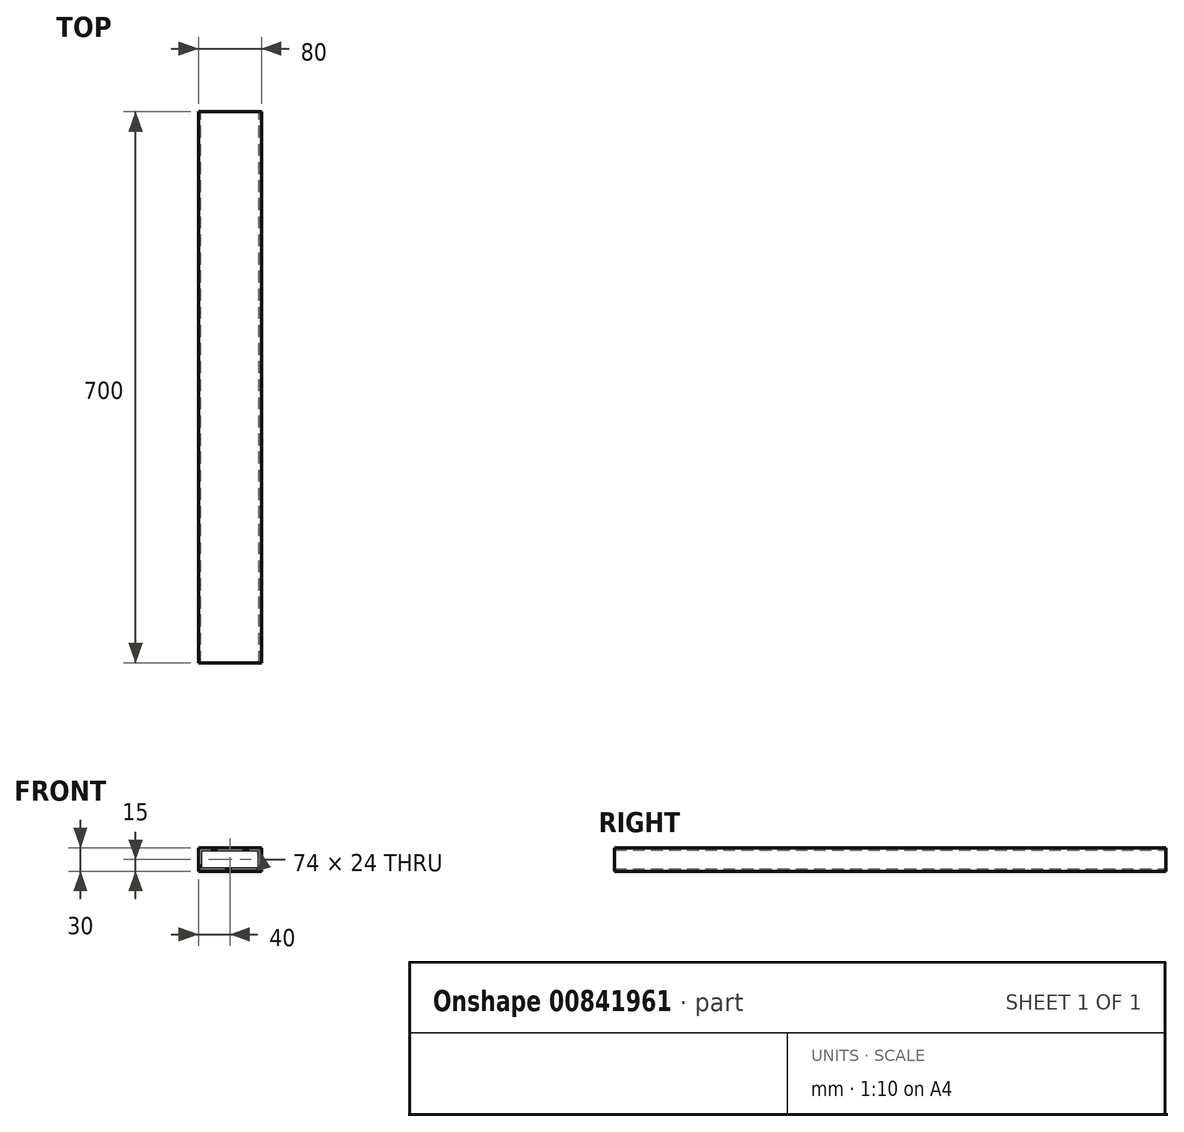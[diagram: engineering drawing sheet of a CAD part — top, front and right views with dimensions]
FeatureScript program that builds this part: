
annotation { "Feature Type Name" : "Feature", "Feature Type Description" : "" }
export const myFeature = defineFeature(function(context is Context, id is Id, definition is map)
    precondition{}
    {
        {
            var Q0;
            Q0=qCreatedBy(makeId("Front.planeOp"),FACE);
            var sketch = newSketch(context, id + "F0", { "sketchPlane" : qUnion([Q0])});
            skLineSegment(sketch, "E0.bottom", {"start": v(-40, 15) * mm, "end": v(40, 15) * mm});
            skLineSegment(sketch, "E0.top", {"start": v(-40, -15) * mm, "end": v(40, -15) * mm});
            skLineSegment(sketch, "E0.left", {"start": v(-40, 15) * mm, "end": v(-40, -15) * mm});
            skLineSegment(sketch, "E0.right", {"start": v(40, 15) * mm, "end": v(40, -15) * mm});
            skLineSegment(sketch, "E1.0", {"start": v(-37, 12) * mm, "end": v(37, 12) * mm});
            skLineSegment(sketch, "E1.1", {"start": v(-37, 12) * mm, "end": v(-37, -12) * mm});
            skLineSegment(sketch, "E1.2", {"start": v(-37, -12) * mm, "end": v(37, -12) * mm});
            skLineSegment(sketch, "E1.3", {"start": v(37, 12) * mm, "end": v(37, -12) * mm});
            skSolve(sketch);
        }
        {
            var Q0;
            Q0=makeQuery(id+"F0.imprint","IMPRINT",FACE,{"disambiguationData":[TD([[makeQuery(id+"F0.imprint","IMPRINT",EDGE,{"derivedFrom":sQuery(id+"F0.wireOp",EDGE,"E0.bottom")}),-1.0]])]});
            extrude(context, id + "F1", {"entities" : qUnion([Q0]), "endBound" : BoundingType.SYMMETRIC, "depth" : 700 * mm, "offsetDistance" : 25 * mm});
        }
    });
